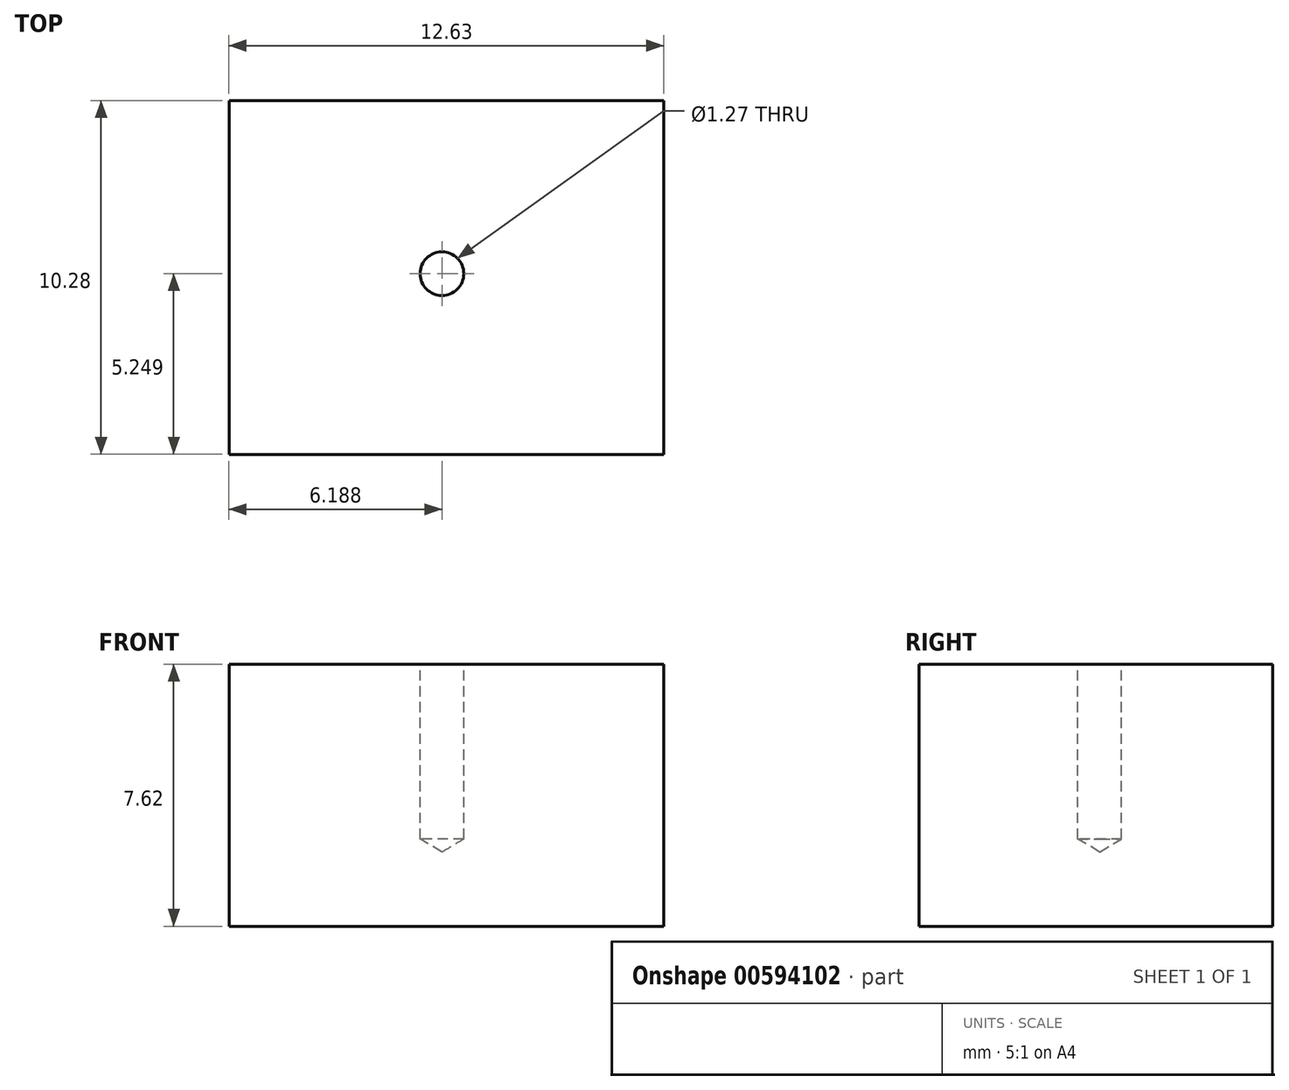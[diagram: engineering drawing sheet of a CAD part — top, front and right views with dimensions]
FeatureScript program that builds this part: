
annotation { "Feature Type Name" : "Feature", "Feature Type Description" : "" }
export const myFeature = defineFeature(function(context is Context, id is Id, definition is map)
    precondition{}
    {
        {
            var Q0;
            Q0=qCreatedBy(makeId("Top.planeOp"),FACE);
            var sketch = newSketch(context, id + "F0", { "sketchPlane" : qUnion([Q0])});
            skLineSegment(sketch, "E0.bottom", {"start": v(-1.63, 5.73) * mm, "end": v(11, 5.73) * mm});
            skLineSegment(sketch, "E0.top", {"start": v(-1.63, -4.55) * mm, "end": v(11, -4.55) * mm});
            skLineSegment(sketch, "E0.left", {"start": v(-1.63, 5.73) * mm, "end": v(-1.63, -4.55) * mm});
            skLineSegment(sketch, "E0.right", {"start": v(11, 5.73) * mm, "end": v(11, -4.55) * mm});
            skSolve(sketch);
        }
        {
            var Q0;
            Q0 = qSketchRegion(id + "F0", true);
            extrude(context, id + "F1", {"entities" : qUnion([Q0]), "depth" : 7.62 * mm, "offsetDistance" : 25.4 * mm});
        }
        {
            var Q0;
            Q0=makeQuery(id+"F1.opExtrude","CAP_FACE",FACE,{"disambiguationData":[OSD([sQuery(id+"F0.wireOp",EDGE,"E0.bottom"),sQuery(id+"F0.wireOp",EDGE,"E0.top"),sQuery(id+"F0.wireOp",EDGE,"E0.left"),sQuery(id+"F0.wireOp",EDGE,"E0.right")])],"isStart":false});
            var sketch = newSketch(context, id + "F2", { "sketchPlane" : qUnion([Q0])});
            skPoint(sketch, "E1", {"position": v(4.56, 0.7) * mm});
            skSolve(sketch);
        }
        {
            var Q0;
            Q0=sQuery(id+"F2.wireOp",VERTEX,"E1");
            var Q1;
            Q1=makeQuery(id+"F1.opExtrude","SWEPT_BODY",BODY,{"disambiguationData":[OSD([sQuery(id+"F0.wireOp",EDGE,"E0.bottom"),sQuery(id+"F0.wireOp",EDGE,"E0.top"),sQuery(id+"F0.wireOp",EDGE,"E0.left"),sQuery(id+"F0.wireOp",EDGE,"E0.right")])]});
            hole(context, id + "F3", {"style" : HoleStyle.SIMPLE, "endStyle" : HoleEndStyle.BLIND, "holeDiameter" : 1.27 * mm, "majorDiameter" : 6.35 * mm, "holeDepth" : 5.08 * mm, "isTappedThrough" : true, "tappedDepth" : 21.59 * mm, "tapClearance" : 3, "locations" : qUnion([Q0]), "scope" : qUnion([Q1])});
        }
    });
